# Revit family: TY6237
name_source: partatom
category: Sprinklers
revit_build: Autodesk Revit 2016 (Build: 20150220_1215(x64)
units: mm (PartAtom-declared; Revit-internal decimal feet)

## family parameters
Always vertical = Yes
Cut with Voids When Loaded = No
Maintain Annotation Orientation = No
OmniClass Number = 23.65.70.17.11.24
OmniClass Title = Fire Fighting Sprinkler Heads
Part Type = Normal
Room Calculation Point = No
Round Connector Dimension = Use Diameter
Shared = No
Work Plane-Based = No

## types (22) — shared parameters
COBie = Yes
COBie.Component.Name = Sprinklers:Pendent_SIN
COBie.Type = Yes
COBie.Type.AssetType = Fixed
COBie.Type.Category = Pr_70_55_97_84:Sprinklers
COBie.Type.DurationUnit = year
COBie.Type.Manufacturer = Tyco Fire Protection Products
COBie.Type.Material = Bronze
COBie.Type.NominalHeight = 0' - 0"
COBie.Type.NominalLength = 0' - 0"
COBie.Type.NominalWidth = 0' - 0"
COBie.Type.Shape = Cylinder
COBie.Type.WarrantyGuarantorParts = http://tycofsbp.com
Coverage = Extended
K-Factor = 13.8732
Manufacturer = Tyco Fire Protection Products
Manufacturer URL = www.tyco-fire.com
Model = EC-14
Nominal Diameter 1 = 1"
Orifice = Extra Large
Orifice Size = 0"
Outside Diameter 1 = 1"
Response = Quick
SIN No = TY6237
Takeout 1 = 2"
Technical Data Sheet No = TFP220
zero-valued in all types: COBie.Type.ReplacementCost, Style Id

## per-type parameters (varying)
| type | COBie.Component.Description | COBie.Type.Colour | COBie.Type.Finish | COBie.Type.ModelNumber | COBie.Type.ModelReference | COBie.Type.Size | Part No | Temperature Rating |
| EC-14 Wet Pendent_Yellow_135  57.2°C K200 DN20 NPT Br_51-895-1-135 | EC-14 Wet Pendent  57.2°C K200 DN20 NPT Br | Yellow | Natural Brass | 51-895-1-135 | EC-14 Wet Pendent  57.2°C K200 DN20 NPT Br | 3/4"(DN20) | 51-895-1-135 | 135 °F |
| EC-14 Wet Pendent_Yellow_155  68.3°C K200 DN20 NPT Br_51-895-1-155 | EC-14 Wet Pendent  68.3°C K200 DN20 NPT Br | Yellow | Natural Brass | 51-895-1-155 | EC-14 Wet Pendent  68.3°C K200 DN20 NPT Br | 3/4"(DN20) | 51-895-1-155 | 155 °F |
| EC-14 Wet Pendent_Yellow_175  79.4°C K200 DN20 NPT Br_51-895-1-175 | EC-14 Wet Pendent  79.4°C K200 DN20 NPT Br | Yellow | Natural Brass | 51-895-1-175 | EC-14 Wet Pendent  79.4°C K200 DN20 NPT Br | 3/4"(DN20) | 51-895-1-175 | 175 °F |
| EC-14 Wet Pendent_Yellow_200  93.3°C K200 DN20 NPT Br_51-895-1-200 | EC-14 Wet Pendent  93.3°C K200 DN20 NPT Br | Yellow | Natural Brass | 51-895-1-200 | EC-14 Wet Pendent  93.3°C K200 DN20 NPT Br | 3/4"(DN20) | 51-895-1-200 | 200 °F |
| EC-14 Wet Pendent_Yellow_286  141.1°C K200 DN20 NPT Br_51-895-1-286 | EC-14 Wet Pendent  141.1°C K200 DN20 NPT Br | Yellow | Natural Brass | 51-895-1-286 | EC-14 Wet Pendent  141.1°C K200 DN20 NPT Br | 3/4"(DN20) | 51-895-1-286 | 286 °F |
| EC-14 Wet Pendent_White_135  57.2°C K200 DN20 NPT Wh9003_51-895-4-135 | EC-14 Wet Pendent  57.2°C K200 DN20 NPT Wh9003 | White | Signal White | 51-895-4-135 | EC-14 Wet Pendent  57.2°C K200 DN20 NPT Wh9003 | 3/4"(DN20) | 51-895-4-135 | 135 °F |
| EC-14 Wet Pendent_White_155  68.3°C K200 DN20 NPT Wh9003_51-895-4-155 | EC-14 Wet Pendent  68.3°C K200 DN20 NPT Wh9003 | White | Signal White | 51-895-4-155 | EC-14 Wet Pendent  68.3°C K200 DN20 NPT Wh9003 | 3/4"(DN20) | 51-895-4-155 | 155 °F |
| EC-14 Wet Pendent_White_175  79.4°C K200 DN20 NPT Wh9003_51-895-4-175 | EC-14 Wet Pendent  79.4°C K200 DN20 NPT Wh9003 | White | Signal White | 51-895-4-175 | EC-14 Wet Pendent  79.4°C K200 DN20 NPT Wh9003 | 3/4"(DN20) | 51-895-4-175 | 175 °F |
| EC-14 Wet Pendent_White_200  93.3°C K200 DN20 NPT Wh9003_51-895-4-200 | EC-14 Wet Pendent  93.3°C K200 DN20 NPT Wh9003 | White | Signal White | 51-895-4-200 | EC-14 Wet Pendent  93.3°C K200 DN20 NPT Wh9003 | 3/4"(DN20) | 51-895-4-200 | 200 °F |
| EC-14 Wet Pendent_White_286  141.1°C K200 DN20 NPT Wh9003_51-895-4-286 | EC-14 Wet Pendent  141.1°C K200 DN20 NPT Wh9003 | White | Signal White | 51-895-4-286 | EC-14 Wet Pendent  141.1°C K200 DN20 NPT Wh9003 | 3/4"9DN20) | 51-895-4-286 | 286 °F |
| EC-14 Wet Pendent_Black_155   68.3°C K200 DN20 NPT JBlk_51-895-5-155 | EC-14 Wet Pendent_White_155  68.3°C K200 DN20 NPT Wh9003 | Black | Jet Black | 51-895-5-155 | EC-14 Wet Pendent_White_155  68.3°C K200 DN20 NPT Wh9003 | 3/4"(DN20) | 51-895-5-155 | 155 °F |
| EC-14 Wet Pendent_Black_200  68.3°C K200 DN20 NPT JBlk_51-895-5-200 | EC-14 Wet Pendent_Black_155   68.3°C K200 DN20 NPT Wh9003 | Black | Jet Black | 51-895-5-200 | EC-14 Wet Pendent_Black_155   68.3°C K200 DN20 NPT Wh9003 | 3/4"(DN20) | 51-895-5-200 | 155 °F |
| EC-14 Wet Pendent_Gray_135  57.2°C K200 DN20 NPT Lead_51-895-7-135 | EC-14 Wet Pendent  57.2°C K200 DN20 NPT LeadCt | Gray | Lead Coated | 51-895-7-135 | EC-14 Wet Pendent  57.2°C K200 DN20 NPT LeadCt | 3/4"(DN20) | 51-895-7-135 | 135 °F |
| EC-14 Wet Pendent_Gray_155  68.3°C K200 DN20 NPT Lead_51-895-7-155 | EC-14 Wet Pendent  68.3°C K200 DN20 NPT LeadCt | Gray | Lead Coated | 51-895-7-155 | EC-14 Wet Pendent  68.3°C K200 DN20 NPT LeadCt | 3/4"(DN20) | 51-895-7-155 | 155 °F |
| EC-14 Wet Pendent_Gray_175  79.4°C K200 DN20 NPT Lead_51-895-7-175 | EC-14 Wet Pendent  79.4°C K200 DN20 NPT LeadCt | Gray | Lead Coated | 51-895-7-175 | EC-14 Wet Pendent  79.4°C K200 DN20 NPT LeadCt | 3/4"(DN20) | 51-895-7-175 | 175 °F |
| EC-14 Wet Pendent_Gray_200  93.3°C K200 DN20 NPT Lead_51-895-7-200 | EC-14 Wet Pendent  93.3°C K200 DN20 NPT LeadCt | Gray | Lead Coated | 51-895-7-200 | EC-14 Wet Pendent  93.3°C K200 DN20 NPT LeadCt | 3/4"(DN20) | 51-895-7-200 | 200 °F |
| EC-14 Wet Pendent_Gray_286  141.1°C K200 DN20 NPT Lead_51-895-7-286 | EC-14 Wet Pendent  141.1°C K200 DN20 NPT LeadCt | Gray | Lead Coated | 51-895-7-286 | EC-14 Wet Pendent  141.1°C K200 DN20 NPT LeadCt | 3/4"(DN20) | 51-895-7-286 | 286 °F |
| EC-14 Wet Pendent_Silver_135  57.2°C K200 DN20 NPT Chr_51-895-9-135 | EC-14 Wet Pendent  57.2°C K200 DN20 NPT Chr | Silver | Chrome Plated | 51-895-9-135 | EC-14 Wet Pendent  57.2°C K200 DN20 NPT Chr | 3/4"(DN20) | 51-895-9-135 | 135 °F |
| EC-14 Wet Pendent_Silver_155  68.3°C K200 DN20 NPT Chr_51-895-9-155 | EC-14 Wet Pendent  68.3°C K200 DN20 NPT Chr | Silver | Chrome Plated | 51-895-9-155 | EC-14 Wet Pendent  68.3°C K200 DN20 NPT Chr | 3/4"(DN20) | 51-895-9-155 | 155 °F |
| EC-14 Wet Pendent_Silver_175  79.4°C K200 DN20 NPT Chr_51-895-9-175 | EC-14 Wet Pendent  79.4°C K200 DN20 NPT Chr | Silver | Chrome Plated | 51-895-9-175 | EC-14 Wet Pendent  79.4°C K200 DN20 NPT Chr | 3/4"(DN20) | 51-895-9-175 | 175 °F |
| EC-14 Wet Pendent_Silver_200  93.3°C K200 DN20 NPT Chr_51-895-9-200 | EC-14 Wet Pendent  93.3°C K200 DN20 NPT Chr | Silver | Chrome Plated | 51-895-9-200 | EC-14 Wet Pendent  93.3°C K200 DN20 NPT Chr | 3/4"(DN20) | 51-895-9-200 | 200 °F |
| EC-14 Wet Pendent_Silver_286  141.1°C K200 DN20 NPT Chr_51-895-9-286 | EC-14 Wet Pendent  141.1°C K200 DN20 NPT Chr | Silver | Chrome Plated | 51-895-9-286 | EC-14 Wet Pendent  141.1°C K200 DN20 NPT Chr | 3/4"(DN20) | 51-895-9-286 | 286 °F |

note: column(s) folded — value = type name in every type: Description

## geometry (parser evidence)
native form markers: Blend x4, Sweep x52
no freeform markers — native parametric forms only
